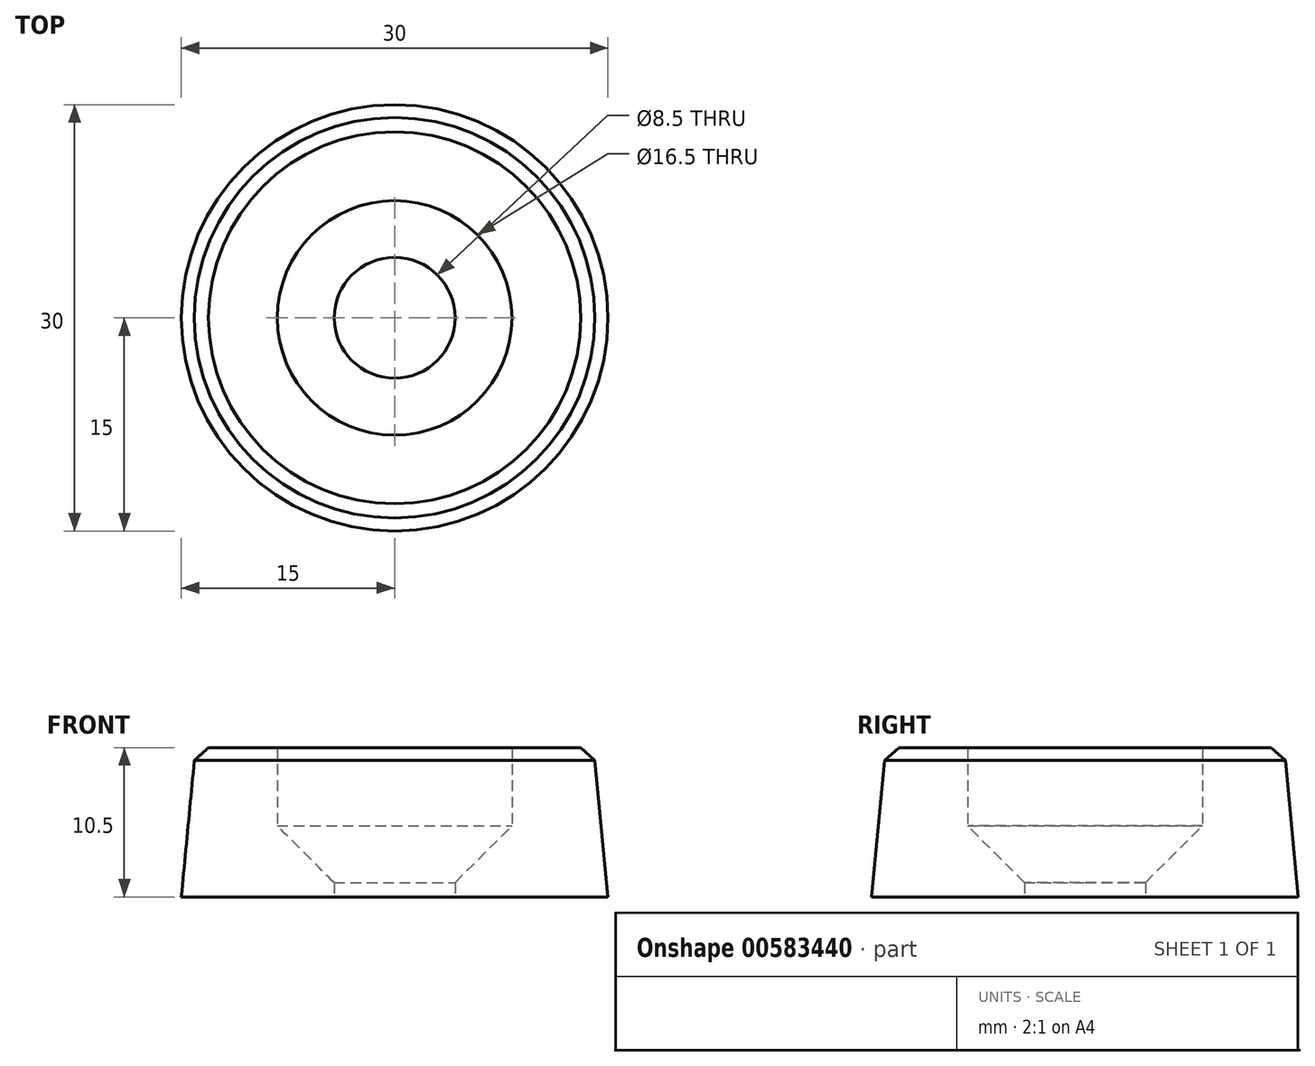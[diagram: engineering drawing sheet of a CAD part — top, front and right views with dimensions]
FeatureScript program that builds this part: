
annotation { "Feature Type Name" : "Feature", "Feature Type Description" : "" }
export const myFeature = defineFeature(function(context is Context, id is Id, definition is map)
    precondition{}
    {
        {
            var Q0;
            Q0=qCreatedBy(makeId("Front.planeOp"),FACE);
            var sketch = newSketch(context, id + "F0", { "sketchPlane" : qUnion([Q0])});
            skLineSegment(sketch, "E0", {"start": v(0, 0) * mm, "end": v(4.25, 0) * mm});
            skLineSegment(sketch, "E1", {"start": v(4.25, 0) * mm, "end": v(4.25, 1) * mm});
            skLineSegment(sketch, "E2", {"start": v(4.25, 1) * mm, "end": v(8.25, 5) * mm});
            skLineSegment(sketch, "E3", {"start": v(8.25, 5) * mm, "end": v(8.25, 10.5) * mm});
            skLineSegment(sketch, "E4", {"start": v(8.25, 10.5) * mm, "end": v(14, 10.5) * mm});
            skLineSegment(sketch, "E5", {"start": v(14, 10.5) * mm, "end": v(15, 0) * mm});
            skLineSegment(sketch, "E6", {"start": v(15, 0) * mm, "end": v(4.25, 0) * mm});
            skLineSegment(sketch, "E7.MirrorCS", {"start": v(0, 0) * mm, "end": v(-4.25, 0) * mm});
            skLineSegment(sketch, "E8.MirrorCS", {"start": v(-8.25, 5) * mm, "end": v(-8.25, 10.5) * mm});
            skLineSegment(sketch, "E9.MirrorCS", {"start": v(-4.25, 1) * mm, "end": v(-8.25, 5) * mm});
            skLineSegment(sketch, "E10.MirrorCS", {"start": v(-8.25, 10.5) * mm, "end": v(-14, 10.5) * mm});
            skLineSegment(sketch, "E11.MirrorCS", {"start": v(-15, 0) * mm, "end": v(-4.25, 0) * mm});
            skLineSegment(sketch, "E12.MirrorCS", {"start": v(-14, 10.5) * mm, "end": v(-15, 0) * mm});
            skLineSegment(sketch, "E13.MirrorCS", {"start": v(-4.25, 0) * mm, "end": v(-4.25, 1) * mm});
            skLineSegment(sketch, "E14", {"start": v(0, 0) * mm, "end": v(0, 10.5) * mm});
            skSolve(sketch);
        }
        {
            var Q0;
            Q0=makeQuery(id+"F0.imprint","IMPRINT",FACE,{"disambiguationData":[TD([[makeQuery(id+"F0.imprint","IMPRINT",EDGE,{"derivedFrom":sQuery(id+"F0.wireOp",EDGE,"E1")}),-1.0]])]});
            var Q1;
            Q1=sQuery(id+"F0.wireOp",EDGE,"E14");
            revolve(context, id + "F1", {"entities" : qUnion([Q0]), "axis" : qUnion([Q1]), "revolveType" : RevolveType.FULL});
        }
        {
            var Q0;
            Q0=makeQuery(id+"F1.opRevolve","SWEPT_EDGE",EDGE,{"disambiguationData":[OSD([sQuery(id+"F0.wireOp",EDGE,"E4"),sQuery(id+"F0.wireOp",EDGE,"E5")])]});
            chamfer(context, id + "F2", {"entities" : qUnion([Q0]), "width" : 1 * mm, "tangentPropagation" : true});
        }
    });
